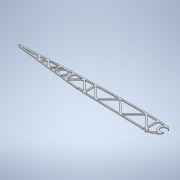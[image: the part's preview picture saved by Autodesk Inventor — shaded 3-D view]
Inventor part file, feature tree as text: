
AUTODESK INVENTOR PART (.ipt)
format: ipt  version: 2022 (Build 260153000, 153)  size: 476,672 bytes
history: native  units: mm
features: extrude x1, sketch x1
ambient origin geometry x8: Origin, YZ Plane, XZ Plane, XY Plane, X Axis, Y Axis, Z Axis, Center Point
bodies: Body1 (feature_tree)
feature tree (2):
  extrude  "Extrusion5"  Depth=10.0mm
  sketch  "Sketch1"  dims[d31=34.456mm d50=368.759386mm d57=16.0mm d69=8.0mm d80=19.0mm d81=16.0mm d82=1.0mm d83=1.0mm d84=1.0mm d85=1.0mm d86=1.0mm d87=0.8mm d88=1.0mm d94=5.0mm d95=5.0mm d105=5.0mm d106=5.0mm d108=2.0mm d114=5.0mm d115=5.0mm d116=24.0mm d117=2.5mm d118=2.5mm d123=2.5mm d124=2.5mm d125=10.0mm d126=24.0mm d127=24.0mm d128=27.0mm d135=0.5mm d139=7.0mm d169=27.0mm d181=45.0deg d185=7.0mm d186=45.0deg d190=7.0mm d191=45.0deg d206=90.0deg d212=90.0deg d215=7.0mm d216=90.0deg d219=7.0mm d220=21.0mm d221=2.0mm d222=0.0mm]
